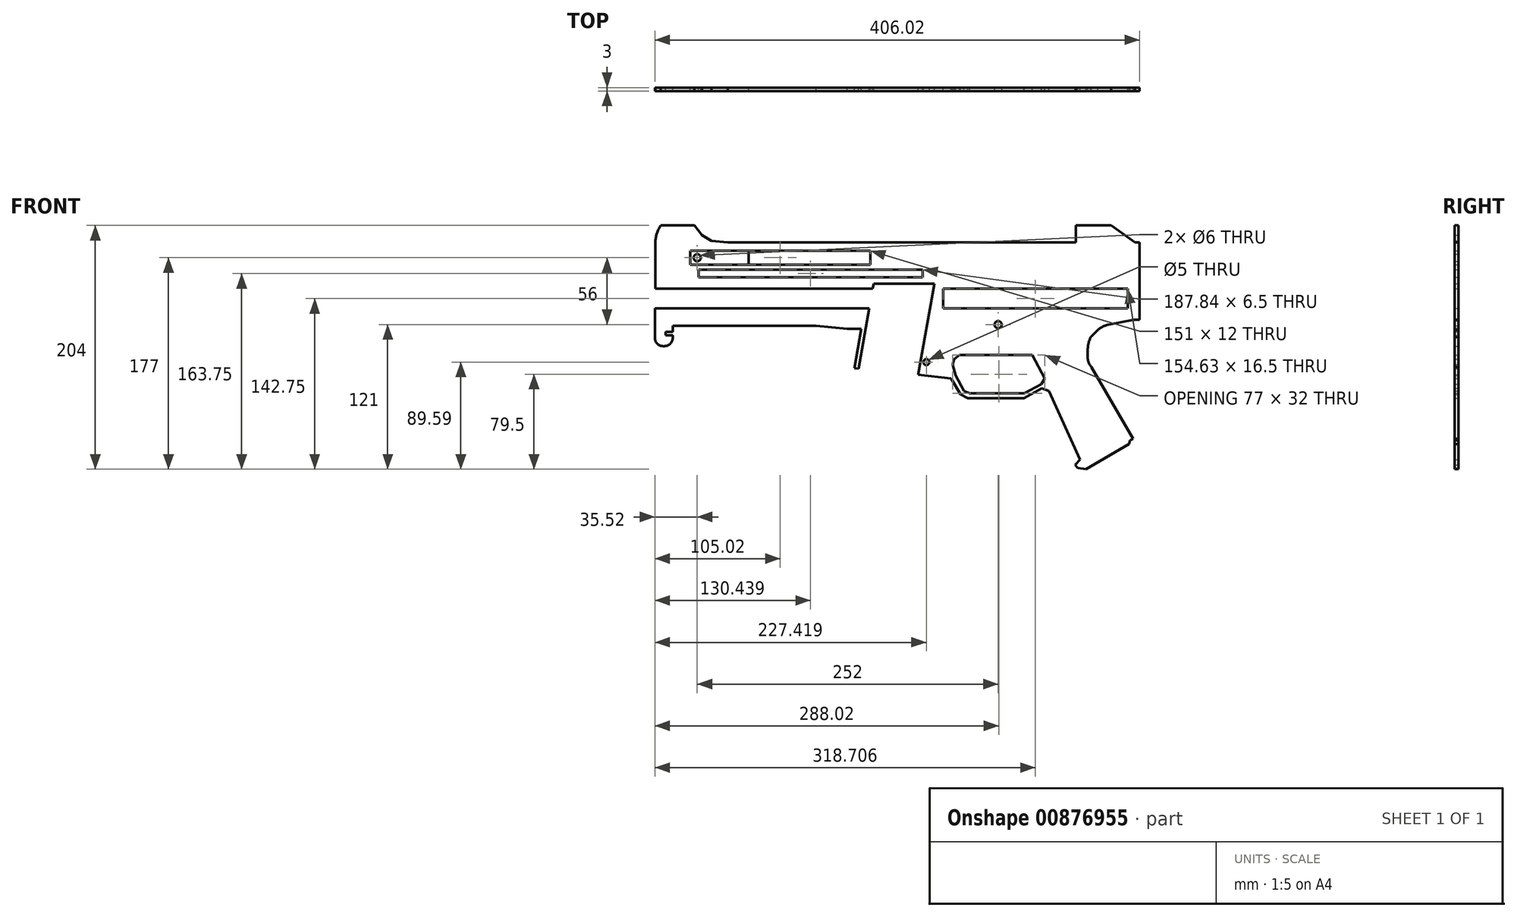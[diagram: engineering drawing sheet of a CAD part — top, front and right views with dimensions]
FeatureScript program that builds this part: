
annotation { "Feature Type Name" : "Feature", "Feature Type Description" : "" }
export const myFeature = defineFeature(function(context is Context, id is Id, definition is map)
    precondition{}
    {
        {
            var Q0;
            Q0=qCreatedBy(makeId("Front.planeOp"),FACE);
            var sketch = newSketch(context, id + "F0", { "sketchPlane" : qUnion([Q0])});
            skLineSegment(sketch, "E0", {"start": v(53.5, -65) * mm, "end": v(53.5, 0) * mm});
            skLineSegment(sketch, "E1", {"start": v(0, 0) * mm, "end": v(0, 14) * mm});
            skLineSegment(sketch, "E2", {"start": v(0, 14) * mm, "end": v(29.55, 14) * mm});
            skPoint(sketch, "E3.visualSharp", {"position": v(0, 14) * mm});
            skPoint(sketch, "E4.visualSharp", {"position": v(29.55, 14) * mm});
            skPoint(sketch, "E5.visualSharp", {"position": v(53.5, 0) * mm});
            skPoint(sketch, "E6.visualSharp", {"position": v(0, 0) * mm});
            skLineSegment(sketch, "E7", {"start": v(53.5, -65) * mm, "end": v(48.5, -65) * mm});
            skLineSegment(sketch, "E8", {"start": v(48.5, -65) * mm, "end": v(27.5, -69) * mm});
            skLineSegment(sketch, "E9", {"start": v(18.5, -73.5) * mm, "end": v(12.5, -79.5) * mm});
            skLineSegment(sketch, "E10", {"start": v(10, -90.5) * mm, "end": v(10, -96.5) * mm});
            skLineSegment(sketch, "E11", {"start": v(13, -104.5) * mm, "end": v(48, -164.5) * mm});
            skLineSegment(sketch, "E12", {"start": v(48, -164.5) * mm, "end": v(45.5, -166) * mm});
            skLineSegment(sketch, "E13", {"start": v(45.5, -166) * mm, "end": v(44.5, -169) * mm});
            skLineSegment(sketch, "E14", {"start": v(44.5, -169) * mm, "end": v(8.5, -190) * mm});
            skLineSegment(sketch, "E15", {"start": v(8.5, -190) * mm, "end": v(1.5, -189) * mm});
            skLineSegment(sketch, "E16", {"start": v(1.5, -189) * mm, "end": v(-0.5, -186.5) * mm});
            skLineSegment(sketch, "E17", {"start": v(-0.5, -186.5) * mm, "end": v(3.5, -182) * mm});
            skLineSegment(sketch, "E18", {"start": v(3.5, -182) * mm, "end": v(-22.5, -124.5) * mm});
            skLineSegment(sketch, "E19", {"start": v(-22.5, -124.5) * mm, "end": v(-28.5, -122.5) * mm});
            skLineSegment(sketch, "E20", {"start": v(-28.5, -122.5) * mm, "end": v(-43.5, -130.5) * mm});
            skLineSegment(sketch, "E21", {"start": v(-43.5, -130.5) * mm, "end": v(-90.5, -130.5) * mm});
            skLineSegment(sketch, "E22", {"start": v(-90.5, -130.5) * mm, "end": v(-96.5, -127.5) * mm});
            skLineSegment(sketch, "E23", {"start": v(-96.5, -127.5) * mm, "end": v(-104.5, -114) * mm});
            skLineSegment(sketch, "E24", {"start": v(-104.5, -114) * mm, "end": v(-131.94, -110.95) * mm});
            skArc(sketch, "E25", {"start": v(10, -90.5) * mm, "mid": v(10.63, -84.86) * mm, "end": v(12.5, -79.5) * mm});
            skArc(sketch, "E26", {"start": v(27.5, -69) * mm, "mid": v(22.69, -70.63) * mm, "end": v(18.5, -73.5) * mm});
            skArc(sketch, "E27", {"start": v(10, -96.5) * mm, "mid": v(10.77, -100.77) * mm, "end": v(13, -104.5) * mm});
            skLineSegment(sketch, "E28", {"start": v(0, 0) * mm, "end": v(-291.5, 0) * mm});
            skLineSegment(sketch, "E29", {"start": v(-291.5, 0) * mm, "end": v(-305, 1) * mm});
            skLineSegment(sketch, "E30", {"start": v(-319.5, 14) * mm, "end": v(-347.5, 14) * mm});
            skLineSegment(sketch, "E31", {"start": v(-345.52, -87) * mm, "end": v(-344.52, -87) * mm});
            skLineSegment(sketch, "E32", {"start": v(-337.52, -70) * mm, "end": v(-217.52, -70) * mm});
            skLineSegment(sketch, "E33", {"start": v(-217.52, -70) * mm, "end": v(-191.52, -72.5) * mm});
            skLineSegment(sketch, "E34", {"start": v(-191.52, -72.5) * mm, "end": v(-179.52, -72.5) * mm});
            skLineSegment(sketch, "E35", {"start": v(-179.52, -72.5) * mm, "end": v(-185.34, -105.5) * mm});
            skArc(sketch, "E36", {"start": v(-352, 0) * mm, "mid": v(-350.85, 7.35) * mm, "end": v(-347.5, 14) * mm});
            skLineSegment(sketch, "E37", {"start": v(-305, 1) * mm, "end": v(-313, 6) * mm});
            skLineSegment(sketch, "E38", {"start": v(-313, 6) * mm, "end": v(-319.5, 14) * mm});
            skLineSegment(sketch, "E39", {"start": v(-352.52, -80) * mm, "end": v(-352.52, -55.5) * mm});
            skLineSegment(sketch, "E40", {"start": v(-352, 0) * mm, "end": v(-352, -39) * mm});
            skLineSegment(sketch, "E41", {"start": v(-26, -114) * mm, "end": v(-29, -119) * mm});
            skLineSegment(sketch, "E42", {"start": v(-29, -119) * mm, "end": v(-43, -126.5) * mm});
            skLineSegment(sketch, "E43", {"start": v(-43, -126.5) * mm, "end": v(-89, -126.5) * mm});
            skLineSegment(sketch, "E44", {"start": v(-89, -126.5) * mm, "end": v(-93.5, -124.5) * mm});
            skLineSegment(sketch, "E45", {"start": v(-93.5, -124.5) * mm, "end": v(-100.5, -111.5) * mm});
            skLineSegment(sketch, "E46", {"start": v(-100.5, -111.5) * mm, "end": v(-103, -102.5) * mm});
            skLineSegment(sketch, "E47", {"start": v(-103, -102.5) * mm, "end": v(-102, -98) * mm});
            skLineSegment(sketch, "E48", {"start": v(-102, -98) * mm, "end": v(-97.5, -94.5) * mm});
            skLineSegment(sketch, "E49", {"start": v(-181.84, -106) * mm, "end": v(-185.34, -105.5) * mm});
            skLineSegment(sketch, "E50", {"start": v(-181.84, -106) * mm, "end": v(-172.93, -55.5) * mm});
            skLineSegment(sketch, "E51", {"start": v(-172.93, -55.5) * mm, "end": v(-352.52, -55.5) * mm});
            skLineSegment(sketch, "E52", {"start": v(-131.94, -110.95) * mm, "end": v(-122.16, -55.5) * mm});
            skLineSegment(sketch, "E53", {"start": v(43.5, -55.5) * mm, "end": v(43.5, -39) * mm});
            skPoint(sketch, "E54", {"position": v(-317, -13) * mm});
            skPoint(sketch, "E55", {"position": v(-215, -13) * mm});
            skLineSegment(sketch, "E56", {"start": v(-97.5, -94.5) * mm, "end": v(-36.5, -94.5) * mm});
            skPoint(sketch, "E57.visualSharp", {"position": v(-352.52, -87) * mm});
            skArc(sketch, "E57.filletArc", {"start": v(-352.52, -80) * mm, "mid": v(-350.47, -84.95) * mm, "end": v(-345.52, -87) * mm});
            skPoint(sketch, "E58.visualSharp", {"position": v(-337.52, -87) * mm});
            skArc(sketch, "E58.filletArc", {"start": v(-344.52, -87) * mm, "mid": v(-339.57, -84.95) * mm, "end": v(-337.52, -80) * mm});
            skLineSegment(sketch, "E59.bottom", {"start": v(-316, -23) * mm, "end": v(-128.16, -23) * mm});
            skLineSegment(sketch, "E59.top", {"start": v(-316, -29.5) * mm, "end": v(-128.16, -29.5) * mm});
            skLineSegment(sketch, "E59.left", {"start": v(-316, -23) * mm, "end": v(-316, -29.5) * mm});
            skLineSegment(sketch, "E59.right", {"start": v(-128.16, -23) * mm, "end": v(-128.16, -29.5) * mm});
            skPoint(sketch, "E60", {"position": v(-323, -7) * mm});
            skPoint(sketch, "E61", {"position": v(-209, -7) * mm});
            skLineSegment(sketch, "E62.bottom", {"start": v(-323, -7) * mm, "end": v(-172, -7) * mm});
            skLineSegment(sketch, "E62.top", {"start": v(-323, -19) * mm, "end": v(-172, -19) * mm});
            skLineSegment(sketch, "E62.left", {"start": v(-323, -7) * mm, "end": v(-323, -19) * mm});
            skLineSegment(sketch, "E62.right", {"start": v(-172, -7) * mm, "end": v(-172, -19) * mm});
            skPoint(sketch, "E63", {"position": v(-121.16, -2.5) * mm});
            skLineSegment(sketch, "E64.bottom", {"start": v(-315.75, -23.25) * mm, "end": v(-230.41, -23.25) * mm, "construction": true});
            skLineSegment(sketch, "E64.top", {"start": v(-315.75, -29.25) * mm, "end": v(-230.41, -29.25) * mm, "construction": true});
            skLineSegment(sketch, "E64.left", {"start": v(-315.75, -23.25) * mm, "end": v(-315.75, -29.25) * mm, "construction": true});
            skLineSegment(sketch, "E64.right", {"start": v(-230.41, -23.25) * mm, "end": v(-230.41, -29.25) * mm, "construction": true});
            skLineSegment(sketch, "E65", {"start": v(-26, -114) * mm, "end": v(-36.5, -94.5) * mm});
            skLineSegment(sketch, "E66", {"start": v(-119.21, -38.77) * mm, "end": v(-118.5, -34.77) * mm});
            skLineSegment(sketch, "E67", {"start": v(-170.03, -39) * mm, "end": v(-169.28, -34.77) * mm});
            skLineSegment(sketch, "E68", {"start": v(-169.28, -34.77) * mm, "end": v(-118.5, -34.77) * mm});
            skLineSegment(sketch, "E69", {"start": v(-352, -39) * mm, "end": v(-170.03, -39) * mm});
            skLineSegment(sketch, "E70", {"start": v(-122.16, -55.5) * mm, "end": v(-119.21, -38.77) * mm});
            skLineSegment(sketch, "E71", {"start": v(-111.13, -39) * mm, "end": v(-111.13, -55.5) * mm});
            skLineSegment(sketch, "E72", {"start": v(43.5, -39) * mm, "end": v(-111.13, -39) * mm});
            skLineSegment(sketch, "E73", {"start": v(-111.13, -55.5) * mm, "end": v(43.5, -55.5) * mm});
            skLineSegment(sketch, "E74.bottom", {"start": v(-86.26, -39.25) * mm, "end": v(-75.26, -39.25) * mm, "construction": true});
            skLineSegment(sketch, "E74.top", {"start": v(-86.26, -55.25) * mm, "end": v(-75.26, -55.25) * mm, "construction": true});
            skLineSegment(sketch, "E74.left", {"start": v(-86.26, -39.25) * mm, "end": v(-86.26, -55.25) * mm, "construction": true});
            skLineSegment(sketch, "E74.right", {"start": v(-75.26, -39.25) * mm, "end": v(-75.26, -55.25) * mm, "construction": true});
            skPoint(sketch, "E75", {"position": v(43.5, -47.25) * mm});
            skLineSegment(sketch, "E76", {"start": v(-104.5, -114) * mm, "end": v(-103, -102.5) * mm, "construction": true});
            skPoint(sketch, "E77", {"position": v(-65, -69) * mm});
            skCircle(sketch, "E78", {"center": v(-65, -69) * mm, "radius": 3 * mm});
            skCircle(sketch, "E79", {"center": v(-125.1, -100.41) * mm, "radius": 2.5 * mm});
            skLineSegment(sketch, "E80", {"start": v(29.55, 14) * mm, "end": v(49.5, 0) * mm});
            skLineSegment(sketch, "E81", {"start": v(49.5, 0) * mm, "end": v(53.5, 0) * mm});
            skPoint(sketch, "E82", {"position": v(-323, -13) * mm});
            skLineSegment(sketch, "E83.bottom", {"start": v(-322.75, -7.25) * mm, "end": v(-274, -7.25) * mm});
            skLineSegment(sketch, "E83.top", {"start": v(-322.75, -18.75) * mm, "end": v(-274, -18.75) * mm});
            skLineSegment(sketch, "E83.left", {"start": v(-322.75, -7.25) * mm, "end": v(-322.75, -18.75) * mm});
            skLineSegment(sketch, "E83.right", {"start": v(-274, -7.25) * mm, "end": v(-274, -18.75) * mm});
            skCircle(sketch, "E84", {"center": v(-317, -13) * mm, "radius": 3 * mm});
            skPoint(sketch, "E85", {"position": v(-314, -13) * mm});
            skLineSegment(sketch, "E86", {"start": v(-337.52, -70) * mm, "end": v(-337.52, -75) * mm});
            skLineSegment(sketch, "E87", {"start": v(-337.52, -75) * mm, "end": v(-343.52, -75) * mm});
            skLineSegment(sketch, "E88", {"start": v(-343.52, -75) * mm, "end": v(-343.52, -78) * mm});
            skLineSegment(sketch, "E89", {"start": v(-343.52, -78) * mm, "end": v(-337.52, -78) * mm});
            skLineSegment(sketch, "E90", {"start": v(-337.52, -78) * mm, "end": v(-337.52, -80) * mm});
            skSolve(sketch);
        }
        {
            var Q0;
            Q0=qSketchRegion(id+"F0",true);
            var Q1;
            Q1=makeQuery(id+"F0.imprint","IMPRINT",FACE,{"disambiguationData":[TD([[makeQuery(id+"F0.imprint","IMPRINT",EDGE,{"derivedFrom":sQuery(id+"F0.wireOp",EDGE,"E64.bottom")}),-1.0]])]});
            var Q2;
            Q2=makeQuery(id+"F0.imprint","IMPRINT",FACE,{"disambiguationData":[TD([[makeQuery(id+"F0.imprint","IMPRINT",EDGE,{"derivedFrom":sQuery(id+"F0.wireOp",EDGE,"E74.bottom")}),-1.0]])]});
            var Q3;
            Q3=makeQuery(id+"F0.imprint","IMPRINT",FACE,{"disambiguationData":[TD([[makeQuery(id+"F0.imprint","IMPRINT",EDGE,{"derivedFrom":sQuery(id+"F0.wireOp",EDGE,"E83.bottom")}),-1.0]])]});
            extrude(context, id + "F1", {"entities" : qUnion([Q0, Q1, Q2, Q3]), "depth" : 3 * mm, "offsetDistance" : 25 * mm});
        }
    });
